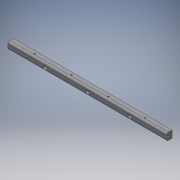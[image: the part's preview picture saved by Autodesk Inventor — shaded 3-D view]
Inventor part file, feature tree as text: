
AUTODESK INVENTOR PART (.ipt)
format: ipt  version: 2019 (Build 230136000, 136)  size: 165,376 bytes
history: native  units: in
note: dims shown in document units (in); Inventor stores cm internally (conversion verified against a paired STEP export)
features: extrude x6, sketch x6, other x2, reference x1, projected_geometry x1, helix x1
ambient origin geometry x8: Origin, YZ Plane, XZ Plane, XY Plane, X Axis, Y Axis, Z Axis, Center Point
bodies: Solid1 (feature_tree)
feature tree (17):
  extrude  "Extrusion1"  Depth=0.5906in TaperAngle=0.0deg
  extrude  "Extrusion2"  Depth=3.937in
  extrude  "Extrusion3"  Depth=3.937in
  extrude  "Extrusion4"  Depth=0.3937in TaperAngle=0.0deg
  extrude  "Extrusion5"  Depth=16.9291in
  extrude  "Extrusion6"  Depth=0.5906in
  sketch  "Sketch1"  dims[d1=0.7874in d2=0.5906in d3=0.0in]
  reference  "Reference1"
  sketch  "Sketch2"  dims[d4=0.1969in d5=3.937in]
  sketch  "Sketch3"  dims[d6=0.1969in d7=3.937in]
  sketch  "Sketch4"  dims[d8=0.1969in d9=0.3937in d10=0.0in]
  sketch  "Sketch5"  dims[d11=16.9291in d12=0.4331in]
  projected_geometry  "Projected Loop1"
  sketch  "Sketch6"  dims[d13=0.4331in d14=0.4331in d15=0.2362in d16=0.0in d17=0.1654in d18=0.1575in d19=0.5906in d20=0.0in d21=0.5906in d22=0.0in d23=0.1378in d24=1.5748in d26=3.937in d27=0.3937in d29=1.0in d31=2.5591in d32=0.5906in d33=0.0in]
  other  "<userpath>\Documents\CAD Files\Helix DLP\Helix DLP.iam"
  helix  "Helix DLP.iam"  [1 undecoded]
  other  "Tank2:1"
note: 1 required parameter value undecoded (feature->parameter linkage not recoverable at this tier; creation-order binding heuristic only, values carry confidence <= 0.55)
